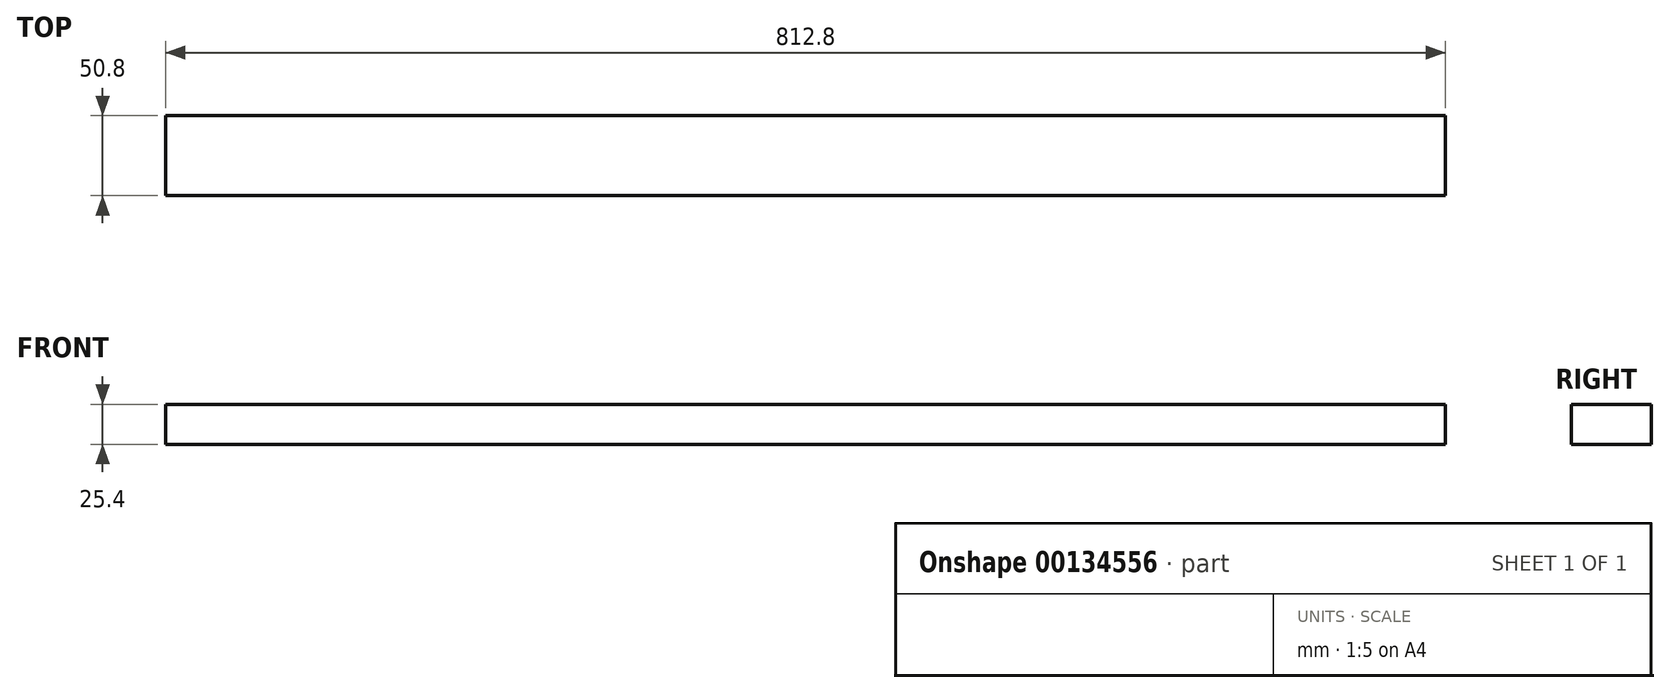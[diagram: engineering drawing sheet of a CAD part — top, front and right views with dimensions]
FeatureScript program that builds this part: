
annotation { "Feature Type Name" : "Feature", "Feature Type Description" : "" }
export const myFeature = defineFeature(function(context is Context, id is Id, definition is map)
    precondition{}
    {
        {
            var Q0;
            Q0=qCreatedBy(makeId("Top.planeOp"),FACE);
            var sketch = newSketch(context, id + "F0", { "sketchPlane" : qUnion([Q0])});
            skLineSegment(sketch, "E0", {"start": v(-12.63, 3.23) * mm, "end": v(800.17, 3.23) * mm});
            skLineSegment(sketch, "E1", {"start": v(800.17, 3.23) * mm, "end": v(800.17, -47.57) * mm});
            skLineSegment(sketch, "E2", {"start": v(800.17, -47.57) * mm, "end": v(-12.63, -47.57) * mm});
            skLineSegment(sketch, "E3", {"start": v(-12.63, -47.57) * mm, "end": v(-12.63, 3.23) * mm});
            skSolve(sketch);
        }
        {
            var Q0;
            Q0=makeQuery(id+"F0.imprint","IMPRINT",FACE,{"disambiguationData":[TD([[makeQuery(id+"F0.imprint","IMPRINT",EDGE,{"derivedFrom":sQuery(id+"F0.wireOp",EDGE,"E0")}),-1.0]])]});
            extrude(context, id + "F1", {"entities" : qUnion([Q0]), "depth" : 25.4 * mm});
        }
    });
